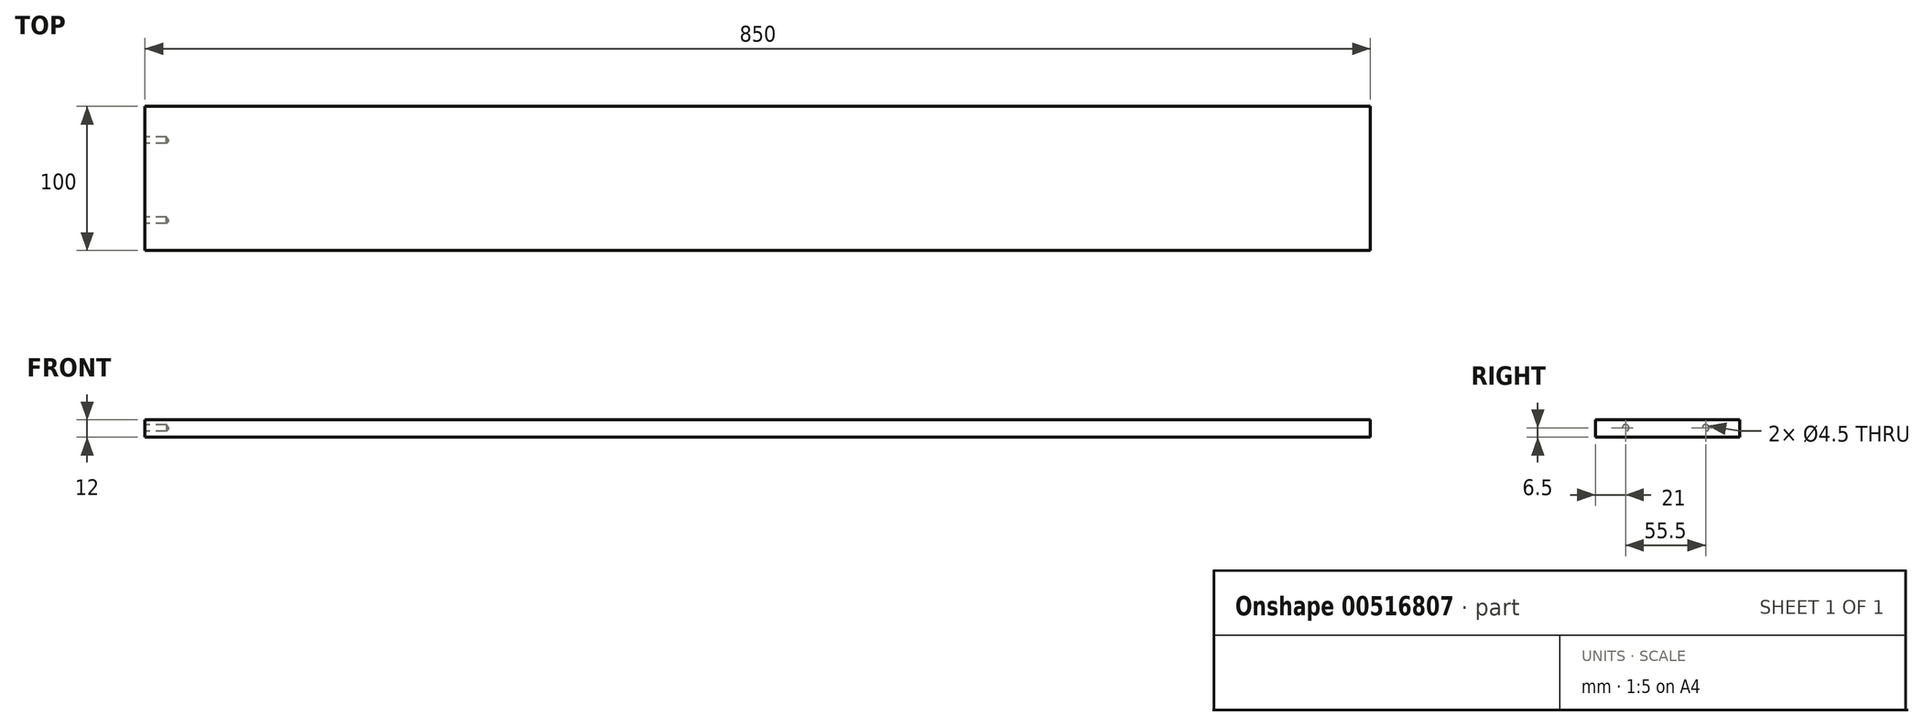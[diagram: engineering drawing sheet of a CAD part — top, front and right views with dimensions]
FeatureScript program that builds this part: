
annotation { "Feature Type Name" : "Feature", "Feature Type Description" : "" }
export const myFeature = defineFeature(function(context is Context, id is Id, definition is map)
    precondition{}
    {
        {
            var Q0;
            Q0=qCreatedBy(makeId("Top.planeOp"),FACE);
            var sketch = newSketch(context, id + "F0", { "sketchPlane" : qUnion([Q0])});
            skLineSegment(sketch, "E0.bottom", {"start": v(0, 0) * mm, "end": v(850, 0) * mm});
            skLineSegment(sketch, "E0.top", {"start": v(0, -100) * mm, "end": v(850, -100) * mm});
            skLineSegment(sketch, "E0.left", {"start": v(0, 0) * mm, "end": v(0, -100) * mm});
            skLineSegment(sketch, "E0.right", {"start": v(850, 0) * mm, "end": v(850, -100) * mm});
            skSolve(sketch);
        }
        {
            var Q0;
            Q0=makeQuery(id+"F0.imprint","IMPRINT",FACE,{"disambiguationData":[TD([[makeQuery(id+"F0.imprint","IMPRINT",EDGE,{"derivedFrom":sQuery(id+"F0.wireOp",EDGE,"E0.bottom")}),-1.0]])]});
            extrude(context, id + "F1", {"entities" : qUnion([Q0]), "depth" : 12 * mm, "offsetDistance" : 25 * mm});
        }
        {
            var Q0;
            Q0=makeQuery(id+"F1.opExtrude","SWEPT_FACE",FACE,{"disambiguationData":[OSD([sQuery(id+"F0.wireOp",EDGE,"E0.left")])]});
            var sketch = newSketch(context, id + "F2", { "sketchPlane" : qUnion([Q0])});
            skCircle(sketch, "E1", {"center": v(23.5, 6.5) * mm, "radius": 2.5 * mm});
            skCircle(sketch, "E2", {"center": v(79, 6.5) * mm, "radius": 2.5 * mm});
            skSolve(sketch);
        }
        {
            var Q0;
            Q0=sQuery(id+"F2.wireOp",VERTEX,"E1.center");
            var Q1;
            Q1=sQuery(id+"F2.wireOp",VERTEX,"E2.center");
            var Q2;
            Q2=makeQuery(id+"F1.opExtrude","SWEPT_BODY",BODY,{"disambiguationData":[OSD([sQuery(id+"F0.wireOp",EDGE,"E0.bottom"),sQuery(id+"F0.wireOp",EDGE,"E0.top"),sQuery(id+"F0.wireOp",EDGE,"E0.left"),sQuery(id+"F0.wireOp",EDGE,"E0.right")])]});
            hole(context, id + "F3", {"style" : HoleStyle.SIMPLE, "endStyle" : HoleEndStyle.BLIND, "standardTappedOrClearance" : lookupTablePath({ "standard" : "ISO", "engagement" : "75%", "pitch" : "0.5 mm", "size" : "M5", "type" : "Tapped" }), "standardBlindInLast" : lookupTablePath({ "standard" : "ISO", "engagement" : "75%", "pitch" : "0.5 mm", "size" : "M5", "type" : "Tapped" }), "holeDiameter" : 4.5 * mm, "showTappedDepth" : true, "holeDepth" : 15 * mm, "isTappedThrough" : true, "tappedDepth" : 13.5 * mm, "tapClearance" : 3, "locations" : qUnion([Q0, Q1]), "scope" : qUnion([Q2]), "majorDiameter" : 5 * mm});
        }
    });
